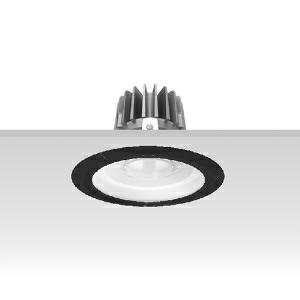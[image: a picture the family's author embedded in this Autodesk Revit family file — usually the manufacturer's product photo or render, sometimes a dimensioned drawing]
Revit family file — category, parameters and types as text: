
# Revit family: 3f_filippi_-_3f_reno_bianco_ampio_3f_filippi_-_30341_a01024_-_3f_reno_150_wh_2000-840_wide___vt_bk_ebac
name_source: partatom
category: Lighting Fixtures
units: mm (PartAtom-declared; Revit-internal decimal feet)

## family parameters
Cut with Voids When Loaded = No
Host = Face
Light Source = No
Part Type = Normal
Room Calculation Point = No
Round Connector Dimension = Use Diameter
Shared = No

## types (1)
- 3F Filippi - 3F Reno Bianco Ampio (1 x LED, 1972 lm, 20 W, 4000 K)
    Apparent Load = 20 VA
    Approval mark = CE
    CIE Flux Codes = 74 93 99 100 100
    Color Rendering = 80
    Color Temperature = 4000 K
    Control Gear = Electronic ballast
    Default Elevation = 1800 mm
    Description = ILLUMINOTECHNICAL
Luminous efficiency 100% (DLOR 100%, ULOR 0%).
Initial luminous flux of the luminaire 1972 lm.
Direct symmetric wide distribution.
Installation Interdistance Transv.D = 1.54 x hu - Long.D = 1.54 x hu.
Tabular UGR (CIE 117 - 4H-8H; S=0.25H; 70/50/20): RUG 23.3 - 23.2.
Beam angle: 74° - 73°.
Luminous efficacy 99 lm/W.
Lifetime (L90/B10): 30000 h. (tq+25°C)
Lifetime (L85/B10): 50000 h. (tq+25°C)
Lifetime (L70/B10): 80000 h. (tq+25°C)
Sudden decreased luminous flux after 50000 hours: 0% (C0).
Photobiological safety in compliance with IEC/TR 62778: RG0 risk exempt, (IEC 62471).
In compliance with IEC/EN 62722-2-1 - IEC/EN 62717 standards.

SOURCE
Compact LED module 2000/840.
Energy efficiency class (UE 2019/2020 - UE 2019/2015): D.
CIE 13.3 Colour rendering index: CRI >80 (R9 <50%).
IES TM-30 Fidelity Index: Rf = 84 Rg = 95.
CCT nominal colour temperature 4000 K.
Colour initial tolerance (MacAdam): SDCM 3.
Zhaga Book 3 compliant.

MECHANICAL
Passive heat dissipator in die-casting aluminium, oversized, for optimum thermal management of the LED module.
Parabolic element with graduated/concentric rings in white polycarbonate.
Transparent external lens with glossy and satin differentiated surfaces, with a cooling and anti-insect system in methacrylate (PMMA).
Fastening spring clips in stainless steel.
Dimensions: diameter 176 mm, height 111 mm. Weight 0.8 kg.
IP44 protection degree for exposed part, IP20 for recessed part.
Mechanical strength to impacts IK06 (1 joule).
Glow-wire test resistance 650°C.

ELECTRICAL
Wiring on a separate unit.
Halogen Free electronic wiring 230V-50/60Hz, power factor 0.95, THD <25%, constant output current, SELV, class II, 1 driver.
Power of the luminaire 20 W.
ENEC - CE.
SAFE FLICKER: PstLM=<1 and SVM=<0.4 (IEC TR 61547-1 and IEC TR 63158), to ensure a more comfortable and safe light.
Luminaire compliant with EN 60598-2-22 for power supply from a centralised emergency system CPSS (Central Power Supply System), not incorporated in the luminaire - high risk areas excluded. The default power and flux are 100% in AC and 100% in DC.
Ambient temperature from 0°C to +25°C.
Temperature class T6 max 85°C.
Relative humidity UR: <85%.

INSTALLATION
Pull-up recessed fitting.
False ceiling carving: 150 mm.
All accessories dedicated to this product are available on the Catalog and on our website www.3F-Filippi.com.

ACCESSORIES
A01024 - VT transparent glass, tempered, not flammable, locked and in line with the trim, in black polycarbonate.

APPLICATIONS
Environments: architectural, commercial, exhibition areas, transit areas, corridors, shops, display windows, service areas.
In false ceilings with narrow voids.

WARNING
Luminaire designed for disposal/recycling at end-of-life.
Replaceable (LED only) light source by a professional. Replaceable control gear by a professional.
    Height = 0 mm  [stored 0 ft]
    Lamp = 1 x LED
    Lamp Light Flux = 1972 lm
    Lamp Power = 20 W
    Lamp count = 1
    Length = 176 mm
    Lifetime = 50000 h
    Luminous efficacy = 99 lm/W
    Manufacturer = 3F Filippi
    ModVariant = No
    Model = 3F Filippi - 30341+A01024 - 3F Reno 150 WH 2000-840 WIDE + VT BK
    Mounting Place = Ceiling
    Mounting Type = Recessed
    Number of Poles = 1
    OnlyDefault = Yes
    Power Factor = 1
    Product Name = 3F Filippi - 3F Reno Bianco Ampio
    Product group = recessed luminaire
    ProductGroupID = 4
    Protection Class = Protection class II
    Protection Degree = IP 20
    RLX_Detail_Level = 1
    RLX_Emergency_Light_Flux = 0 lm
    RLX_Emergency_Type = 0
    RLX_Emergency_Type_DB = No
    RlxData = <blob elided: 85173 chars, md5=fbfd6139>
    Socket = socket
    Standby Power = 0 W
    System Light Flux = 1972 lm
    System Power = 20 W
    Type Comments = Product without accessories
    Type Image = 3ffilippi_3f_reno_150_wh_d100__a01024.jpg
    URL = http://relux.com
    VarID = ---
    Voltage = 0 V
    Weight = 0.00 kg
    Width = 0 mm  [stored 0 ft]

note: [stored X ft] marks values corroborated as IEEE doubles in the binary element streams (Revit-internal decimal feet)

## geometry (parser evidence)
native form markers: Blend x4, Sweep x11
no freeform markers — native parametric forms only
